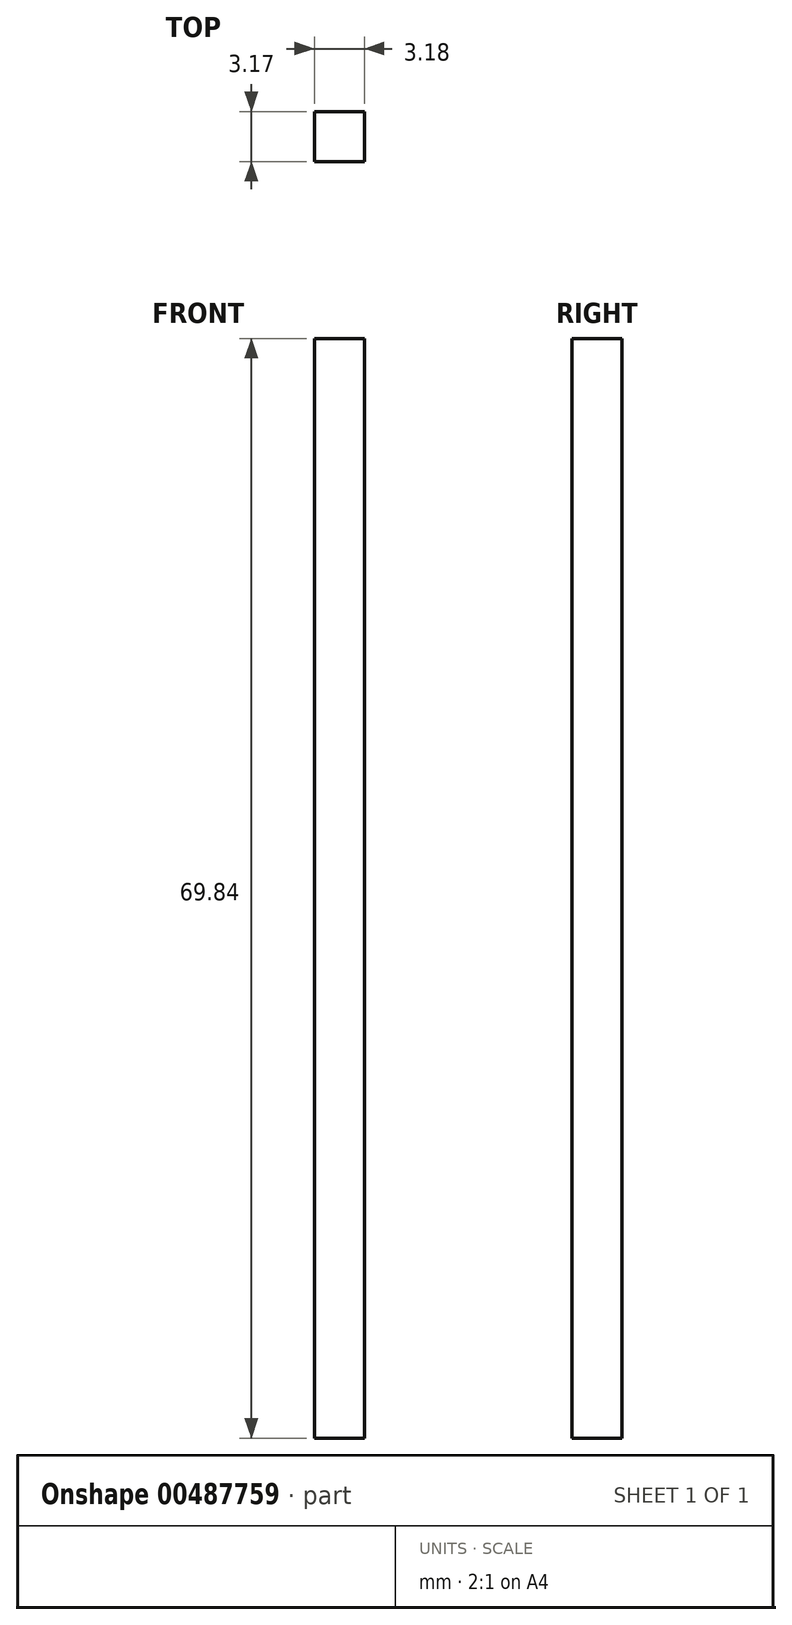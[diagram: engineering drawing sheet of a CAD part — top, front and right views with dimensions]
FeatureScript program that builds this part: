
annotation { "Feature Type Name" : "Feature", "Feature Type Description" : "" }
export const myFeature = defineFeature(function(context is Context, id is Id, definition is map)
    precondition{}
    {
        {
            var Q0;
            Q0=qCreatedBy(makeId("Front.planeOp"),FACE);
            var sketch = newSketch(context, id + "F0", { "sketchPlane" : qUnion([Q0])});
            skLineSegment(sketch, "E0.bottom", {"start": v(1.59, 34.93) * mm, "end": v(-1.59, 34.93) * mm});
            skLineSegment(sketch, "E0.top", {"start": v(1.59, -34.93) * mm, "end": v(-1.59, -34.93) * mm});
            skLineSegment(sketch, "E0.left", {"start": v(1.59, 34.93) * mm, "end": v(1.59, -34.93) * mm});
            skLineSegment(sketch, "E0.right", {"start": v(-1.59, 34.93) * mm, "end": v(-1.59, -34.93) * mm});
            skPoint(sketch, "E0.middle", {"position": v(0, 0) * mm});
            skSolve(sketch);
        }
        {
            var Q0;
            Q0=makeQuery(id+"F0.imprint","IMPRINT",FACE,{"disambiguationData":[TD([[makeQuery(id+"F0.imprint","IMPRINT",EDGE,{"derivedFrom":sQuery(id+"F0.wireOp",EDGE,"E0.bottom")}),1.0]])]});
            extrude(context, id + "F1", {"entities" : qUnion([Q0]), "depth" : 3.17 * mm});
        }
    });
